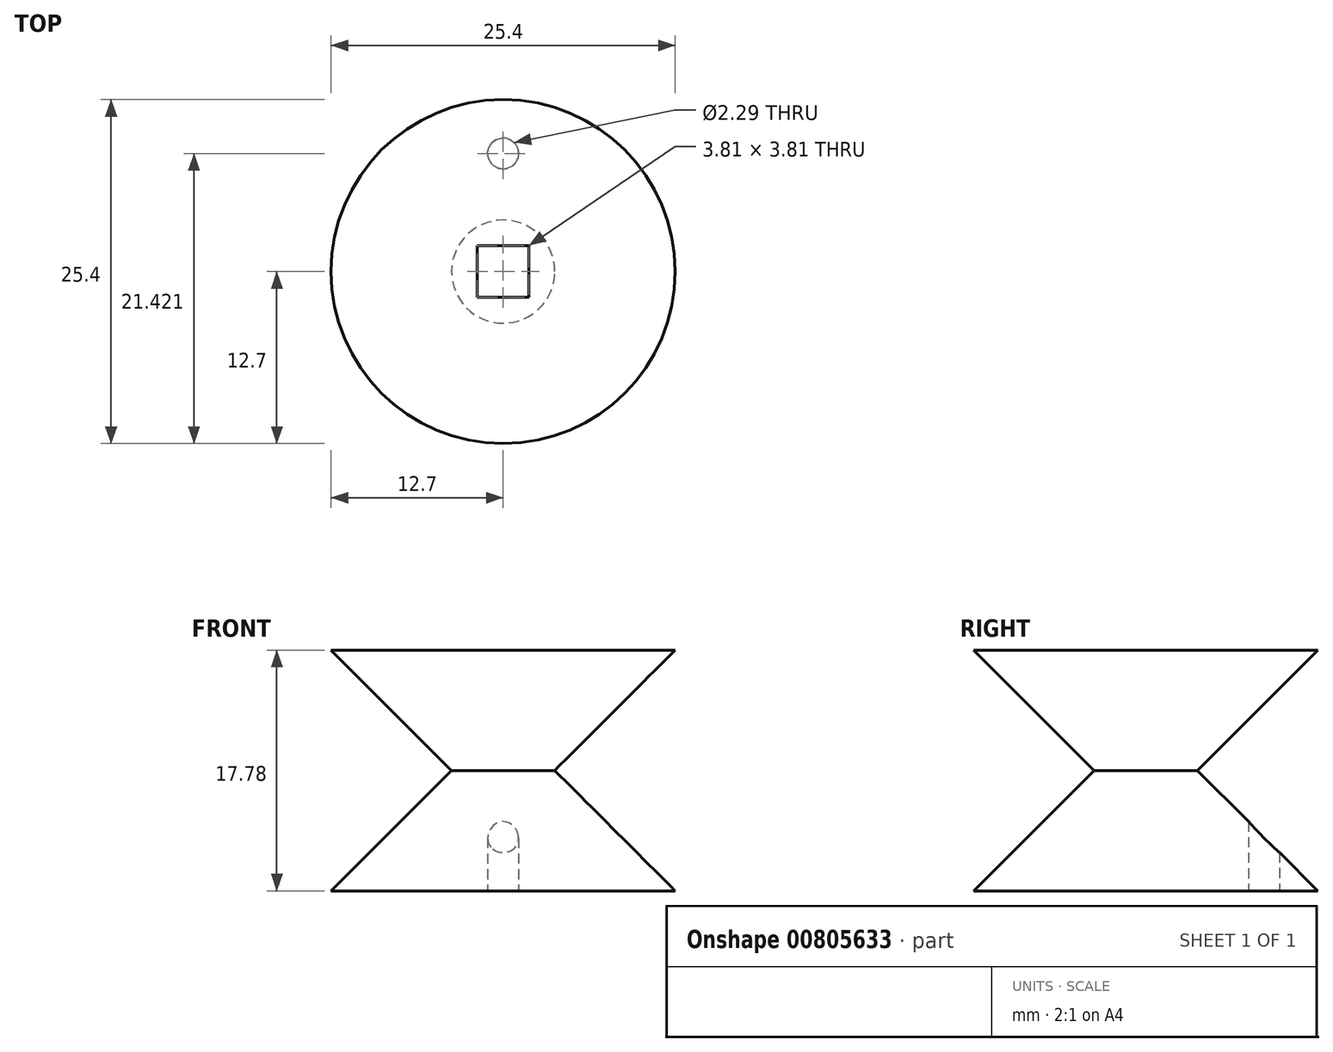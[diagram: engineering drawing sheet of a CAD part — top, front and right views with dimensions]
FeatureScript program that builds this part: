
annotation { "Feature Type Name" : "Feature", "Feature Type Description" : "" }
export const myFeature = defineFeature(function(context is Context, id is Id, definition is map)
    precondition{}
    {
        {
            var Q0;
            Q0=qCreatedBy(makeId("Top.planeOp"),FACE);
            cPlane(context, id + "F0", {"entities" : qUnion([Q0]), "cplaneType" : CPlaneType.OFFSET, "offset" : 8.9 * mm, "width" : 150 * mm, "height" : 150 * mm});
        }
        {
            var Q0;
            Q0=qCreatedBy(makeId("Top.planeOp"),FACE);
            cPlane(context, id + "F1", {"entities" : qUnion([Q0]), "cplaneType" : CPlaneType.OFFSET, "offset" : 8.9 * mm, "oppositeDirection" : true, "width" : 150 * mm, "height" : 150 * mm});
        }
        {
            var Q0;
            Q0=qCreatedBy(id+"F0.planeOp",FACE);
            var sketch = newSketch(context, id + "F2", { "sketchPlane" : qUnion([Q0])});
            skPoint(sketch, "E0.middle", {"position": v(0, 0) * mm});
            skCircle(sketch, "E1", {"center": v(0, 0) * mm, "radius": 12.7 * mm});
            skSolve(sketch);
        }
        {
            var Q0;
            Q0=qCreatedBy(id+"F1.planeOp",FACE);
            var sketch = newSketch(context, id + "F3", { "sketchPlane" : qUnion([Q0])});
            skPoint(sketch, "E2", {"position": v(0, 0) * mm});
            skCircle(sketch, "E3", {"center": v(0, 0) * mm, "radius": 12.7 * mm});
            skSolve(sketch);
        }
        {
            var Q0;
            Q0=qCreatedBy(makeId("Top.planeOp"),FACE);
            var sketch = newSketch(context, id + "F4", { "sketchPlane" : qUnion([Q0])});
            skCircle(sketch, "E4", {"center": v(0, 0) * mm, "radius": 3.81 * mm});
            skSolve(sketch);
        }
        {
            var Q0;
            Q0=makeQuery(id+"F3.imprint","IMPRINT",FACE,{"disambiguationData":[TD([[makeQuery(id+"F3.imprint","IMPRINT",EDGE,{"derivedFrom":sQuery(id+"F3.wireOp",EDGE,"E3")}),1.0]])]});
            var Q1;
            Q1=makeQuery(id+"F4.imprint","IMPRINT",FACE,{"disambiguationData":[TD([[makeQuery(id+"F4.imprint","IMPRINT",EDGE,{"derivedFrom":sQuery(id+"F4.wireOp",EDGE,"E4")}),1.0]])]});
            loft(context, id + "F5", {"sheetProfilesArray" : [{ "sheetProfileEntities" : qUnion([Q0]) }, { "sheetProfileEntities" : qUnion([Q1]) }]});
        }
        {
            var Q1;
            Q1=makeQuery(id+"F2.imprint","IMPRINT",FACE,{"disambiguationData":[TD([[makeQuery(id+"F2.imprint","IMPRINT",EDGE,{"derivedFrom":sQuery(id+"F2.wireOp",EDGE,"E1")}),1.0]])]});
            var Q2;
            Q2=makeQuery(id+"F4.imprint","IMPRINT",FACE,{"disambiguationData":[TD([[makeQuery(id+"F4.imprint","IMPRINT",EDGE,{"derivedFrom":sQuery(id+"F4.wireOp",EDGE,"E4")}),1.0]])]});
            loft(context, id + "F6", {"operationType" : NewBodyOperationType.ADD, "sheetProfilesArray" : [{ "sheetProfileEntities" : qUnion([Q1]) }, { "sheetProfileEntities" : qUnion([Q2]) }]});
        }
        {
            var Q0;
            Q0=qCreatedBy(id+"F0.planeOp",FACE);
            var sketch = newSketch(context, id + "F7", { "sketchPlane" : qUnion([Q0])});
            skLineSegment(sketch, "E5.bottom", {"start": v(1.9, 1.9) * mm, "end": v(-1.9, 1.9) * mm});
            skLineSegment(sketch, "E5.top", {"start": v(1.9, -1.9) * mm, "end": v(-1.9, -1.9) * mm});
            skLineSegment(sketch, "E5.left", {"start": v(1.9, 1.9) * mm, "end": v(1.9, -1.9) * mm});
            skLineSegment(sketch, "E5.right", {"start": v(-1.9, 1.9) * mm, "end": v(-1.9, -1.9) * mm});
            skPoint(sketch, "E5.middle", {"position": v(0, 0) * mm});
            skSolve(sketch);
        }
        {
            var Q0;
            Q0 = qSketchRegion(id + "F7", true);
            extrude(context, id + "F8", {"entities" : qUnion([Q0]), "operationType" : NewBodyOperationType.REMOVE, "oppositeDirection" : true, "depth" : 25.4 * mm, "offsetDistance" : 25.4 * mm});
        }
        {
            var Q0;
            Q0=qCreatedBy(id+"F1.planeOp",FACE);
            var sketch = newSketch(context, id + "F9", { "sketchPlane" : qUnion([Q0])});
            skCircle(sketch, "E6", {"center": v(0, 8.72) * mm, "radius": 1.14 * mm});
            skSolve(sketch);
        }
        {
            var Q0;
            Q0=makeQuery(id+"F9.imprint","IMPRINT",FACE,{"disambiguationData":[TD([[makeQuery(id+"F9.imprint","IMPRINT",EDGE,{"derivedFrom":sQuery(id+"F9.wireOp",EDGE,"E6")}),1.0]])]});
            extrude(context, id + "F10", {"entities" : qUnion([Q0]), "operationType" : NewBodyOperationType.REMOVE, "depth" : 6.86 * mm, "offsetDistance" : 25.4 * mm});
        }
    });
